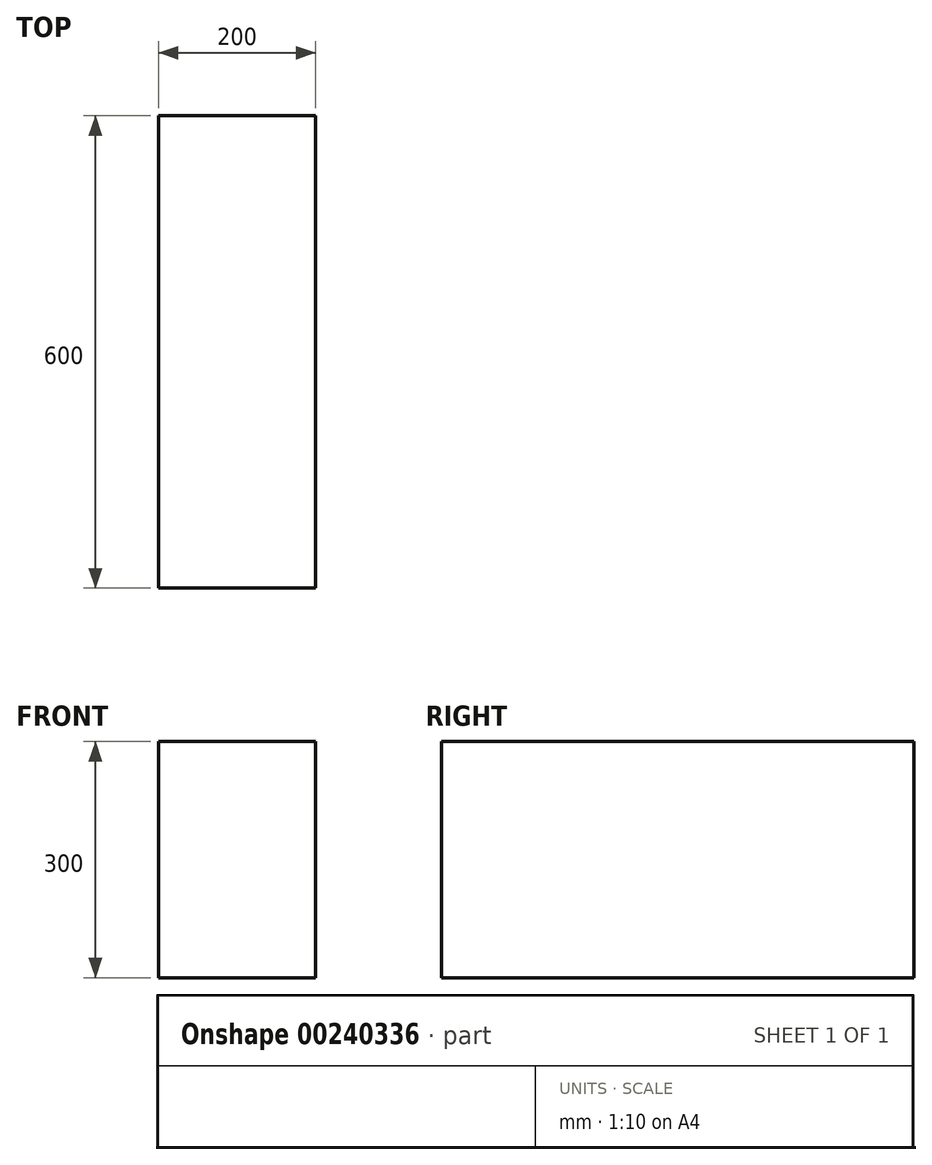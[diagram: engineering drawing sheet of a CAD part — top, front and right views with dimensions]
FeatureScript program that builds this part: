
annotation { "Feature Type Name" : "Feature", "Feature Type Description" : "" }
export const myFeature = defineFeature(function(context is Context, id is Id, definition is map)
    precondition{}
    {
        {
            var Q0;
            Q0=qCreatedBy(makeId("Right.planeOp"),FACE);
            var sketch = newSketch(context, id + "F0", { "sketchPlane" : qUnion([Q0])});
            skLineSegment(sketch, "E0.bottom", {"start": v(300, 150) * mm, "end": v(-300, 150) * mm});
            skLineSegment(sketch, "E0.top", {"start": v(300, -150) * mm, "end": v(-300, -150) * mm});
            skLineSegment(sketch, "E0.left", {"start": v(300, 150) * mm, "end": v(300, -150) * mm});
            skLineSegment(sketch, "E0.right", {"start": v(-300, 150) * mm, "end": v(-300, -150) * mm});
            skPoint(sketch, "E0.middle", {"position": v(0, 0) * mm});
            skSolve(sketch);
        }
        {
            var Q0;
            Q0 = qSketchRegion(id + "F0", true);
            extrude(context, id + "F1", {"entities" : qUnion([Q0]), "endBound" : BoundingType.SYMMETRIC, "depth" : 200 * mm});
        }
    });
